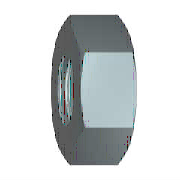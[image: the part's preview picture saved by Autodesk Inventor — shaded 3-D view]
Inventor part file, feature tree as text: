
AUTODESK INVENTOR PART (.ipt)
format: ipt  version: 2021 (Build 250183000, 183)  size: 164,864 bytes
history: native  units: mm (DEFAULTED — no unit token found)
features: sketch x3, chamfer x1, hole x1, other x1, plane x1
ambient origin geometry x7: Origin, YZ Plane, XZ Plane, X Axis, Y Axis, Z Axis, Center Point
bodies: Solid1 (feature_tree), Body (feature_tree)
feature tree (7):
  chamfer  "Chamfer1"  Angle=30.0deg  [1 undecoded]
  hole  "Thread"  [1 undecoded]
  other  "Work Axis1"
  plane  "Work Plane1"
  sketch  "Sketch1"  dims[d0=11.547005mm]
  sketch  "Sketch2"  dims[d1=5.2mm]
  sketch  "Sketch3"  dims[d2=0.0mm d3=30.0deg d4=30.0deg d5=8.9mm d6=8.9mm d7=90.0deg d25=4.917mm d26=6.0mm d27=4.0mm d28=2.0mm d29=14.3117mm d30=8.0mm d31=20.594885mm d8=0.541266mm d9=30.0deg d10=0.541266mm d11=30.0deg d13=0.0mm d14=0.0mm d39=0.0mm d40=0.541266mm d41=0.541266mm d42=0.0mm]
note: 2 required parameter values undecoded (feature->parameter linkage not recoverable at this tier; creation-order binding heuristic only, values carry confidence <= 0.55)
